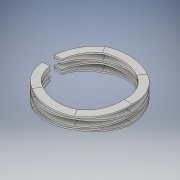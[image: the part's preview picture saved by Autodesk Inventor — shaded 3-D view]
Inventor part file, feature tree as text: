
AUTODESK INVENTOR PART (.ipt)
format: ipt  version: 2018 (Build 220112000, 112)  size: 372,224 bytes
history: native  units: in
note: dims shown in document units (in); Inventor stores cm internally (conversion verified against a paired STEP export)
features: sketch x7, projected_geometry x6, extrude x5, plane x2, pattern_circular x2, mirror x1, direct_edit x1, other x1
ambient origin geometry x8: Origin, YZ Plane, XZ Plane, XY Plane, X Axis, Y Axis, Z Axis, Center Point
bodies: Solid1 (feature_tree)
feature tree (25):
  extrude  "Extrusion1"  Depth=1.73in
  sketch  "Sketch3"  dims[d2=0.552in d3=0.0in d7=2.3622in d9=360.0deg]
  sketch  "Sketch5"  dims[d22=0.5767in d23=0.5765in d24=0.5768in d25=0.045in d26=0.045in d27=0.09in d28=0.045in d29=0.045in d30=0.09in d31=0.045in d32=0.09in]
  plane  "Work Plane1"
  sketch  "Sketch11"  dims[d42=0.002in]
  plane  "Work Plane2"
  extrude  "Extrusion9"  Depth=2.3622in TaperAngle=360.0deg
  mirror  "Mirror6"
  pattern_circular  "Circular Pattern1"  Count=3 Angle=360.0deg
  extrude  "Extrusion10"  Depth=0.3937in TaperAngle=0.0deg
  extrude  "Extrusion11"  Depth=0.3937in TaperAngle=360.0deg
  pattern_circular  "Circular Pattern2"  [2 undecoded]
  extrude  "Extrusion12"  Depth=0.3937in
  direct_edit  "Direct Edit1"
  sketch  "Sketch1"  dims[d0=1.41in d1=1.73in]
  projected_geometry  "Projected Loop10"
  sketch  "Sketch13"  dims[d45=1.1025in]
  projected_geometry  "Projected Loop12"
  sketch  "Sketch14"  dims[d51=1.0in d52=0.0in d53=1.1811in d54=360.0deg]
  projected_geometry  "Projected Loop13"
  projected_geometry  "Projected Loop14"
  projected_geometry  "Projected Loop15"
  projected_geometry  "Projected Loop16"
  sketch  "Sketch15"  dims[d56=1.0in d57=0.0in d58=1.0in d59=0.0in d60=1.1811in d61=360.0deg d63=0.1225in d64=0.1225in d65=1.0in d66=0.0in d67=0.3937in d68=0.3937in d69=0.2597in]
  other  "Scale1"
note: 2 required parameter values undecoded (feature->parameter linkage not recoverable at this tier; creation-order binding heuristic only, values carry confidence <= 0.55)
